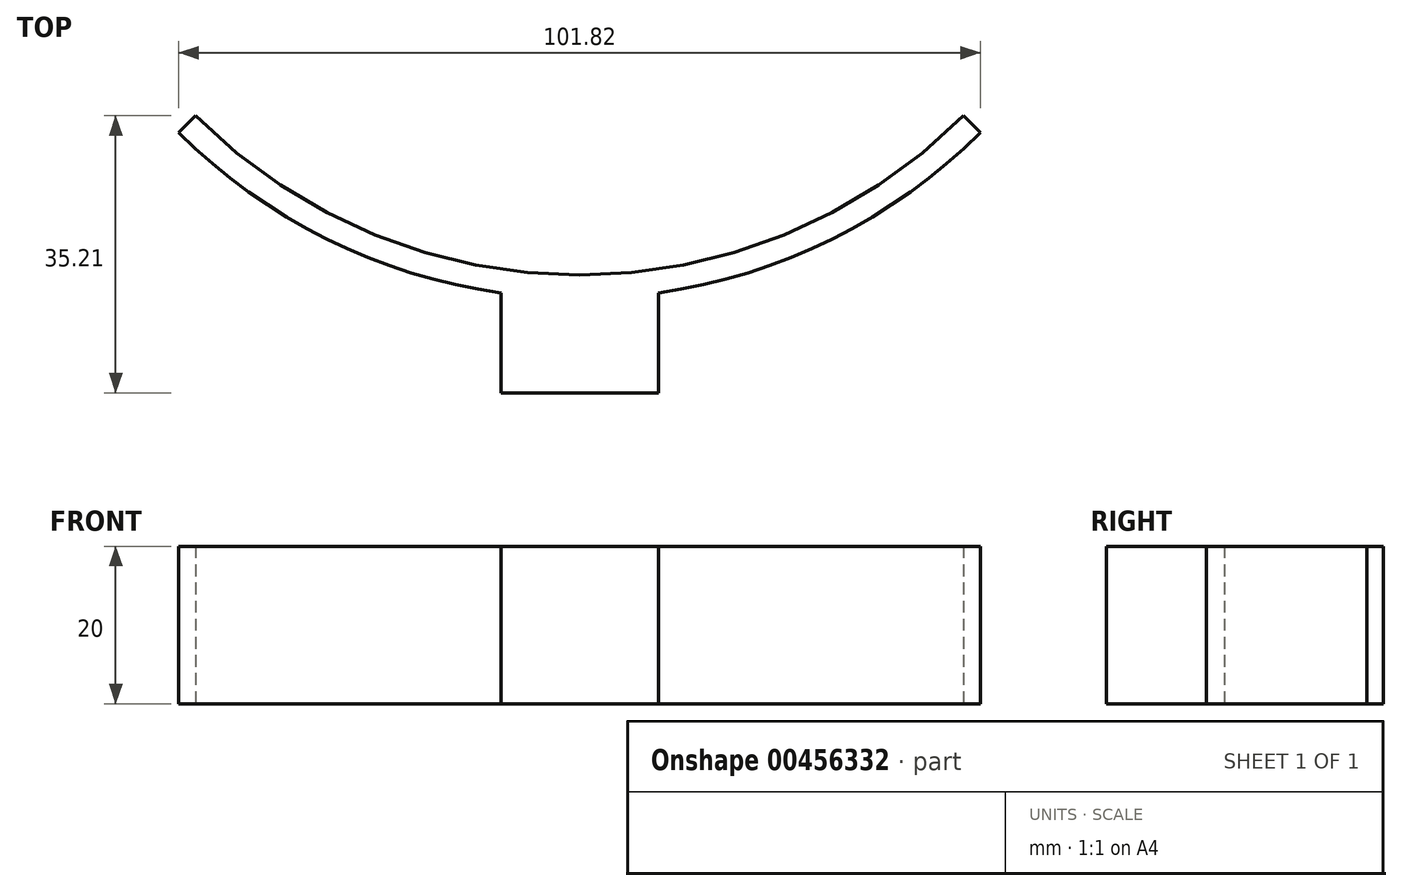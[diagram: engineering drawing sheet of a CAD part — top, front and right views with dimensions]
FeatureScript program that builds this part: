
annotation { "Feature Type Name" : "Feature", "Feature Type Description" : "" }
export const myFeature = defineFeature(function(context is Context, id is Id, definition is map)
    precondition{}
    {
        {
            var Q0;
            Q0=qCreatedBy(makeId("Top.planeOp"),FACE);
            var sketch = newSketch(context, id + "F0", { "sketchPlane" : qUnion([Q0])});
            skArc(sketch, "E0", {"start": v(-69, 0) * mm, "mid": v(0, -69) * mm, "end": v(69, 0) * mm, "construction": true});
            skLineSegment(sketch, "E1", {"start": v(-75.39, -69) * mm, "end": v(83.47, -69) * mm, "construction": true});
            skLineSegment(sketch, "E2", {"start": v(0, 0) * mm, "end": v(0, -69) * mm, "construction": true});
            skArc(sketch, "E3", {"start": v(10, -69) * mm, "mid": v(0, -59) * mm, "end": v(-10, -69) * mm, "construction": true});
            skLineSegment(sketch, "E4", {"start": v(10, -69) * mm, "end": v(10, -84) * mm});
            skLineSegment(sketch, "E5", {"start": v(10, -84) * mm, "end": v(-10, -84) * mm});
            skLineSegment(sketch, "E6", {"start": v(-10, -84) * mm, "end": v(-10, -69) * mm});
            skLineSegment(sketch, "E7", {"start": v(0, 0) * mm, "end": v(48.8, -48.8) * mm, "construction": true});
            skLineSegment(sketch, "E8", {"start": v(48.8, -48.8) * mm, "end": v(0, -48.8) * mm, "construction": true});
            skLineSegment(sketch, "E9", {"start": v(48.8, -48.8) * mm, "end": v(48.8, 0) * mm, "construction": true});
            skLineSegment(sketch, "E10.MirrorCS", {"start": v(0, 0) * mm, "end": v(-48.8, -48.8) * mm, "construction": true});
            skLineSegment(sketch, "E11", {"start": v(48.8, -48.8) * mm, "end": v(50.91, -50.91) * mm});
            skArc(sketch, "E12", {"start": v(50.91, -50.91) * mm, "mid": v(0, -72) * mm, "end": v(-50.91, -50.91) * mm, "construction": true});
            skLineSegment(sketch, "E13.MirrorCS", {"start": v(-48.8, -48.8) * mm, "end": v(-50.91, -50.91) * mm});
            skLineSegment(sketch, "E14", {"start": v(-10, -69) * mm, "end": v(10, -69) * mm});
            skArc(sketch, "E15", {"start": v(48.8, -48.8) * mm, "mid": v(0, -69) * mm, "end": v(-48.8, -48.8) * mm});
            skArc(sketch, "E16", {"start": v(10, -71.3) * mm, "mid": v(32.12, -64.44) * mm, "end": v(50.91, -50.91) * mm});
            skArc(sketch, "E17", {"start": v(-50.91, -50.91) * mm, "mid": v(-32.12, -64.44) * mm, "end": v(-10, -71.3) * mm});
            skSolve(sketch);
        }
        {
            var Q0;
            {var subQ1=sQuery(id+"F0.wireOp",EDGE,"E11");Q0=makeQuery(id+"F0.imprint","IMPRINT",FACE,{"disambiguationData":[TD([[makeQuery(id+"F0.imprint","IMPRINT",EDGE,{"derivedFrom":subQ1}),-1.0]])]});}
            var Q1;
            {var subQ1=sQuery(id+"F0.wireOp",EDGE,"E5");Q1=makeQuery(id+"F0.imprint","IMPRINT",FACE,{"disambiguationData":[TD([[makeQuery(id+"F0.imprint","IMPRINT",EDGE,{"derivedFrom":subQ1}),-1.0]])]});}
            var Q2;
            {var subQ1=sQuery(id+"F0.wireOp",EDGE,"E13.MirrorCS");Q2=makeQuery(id+"F0.imprint","IMPRINT",FACE,{"disambiguationData":[TD([[makeQuery(id+"F0.imprint","IMPRINT",EDGE,{"derivedFrom":subQ1}),1.0]])]});}
            extrude(context, id + "F1", {"entities" : qUnion([Q0, Q1, Q2]), "depth" : 20 * mm});
        }
    });
